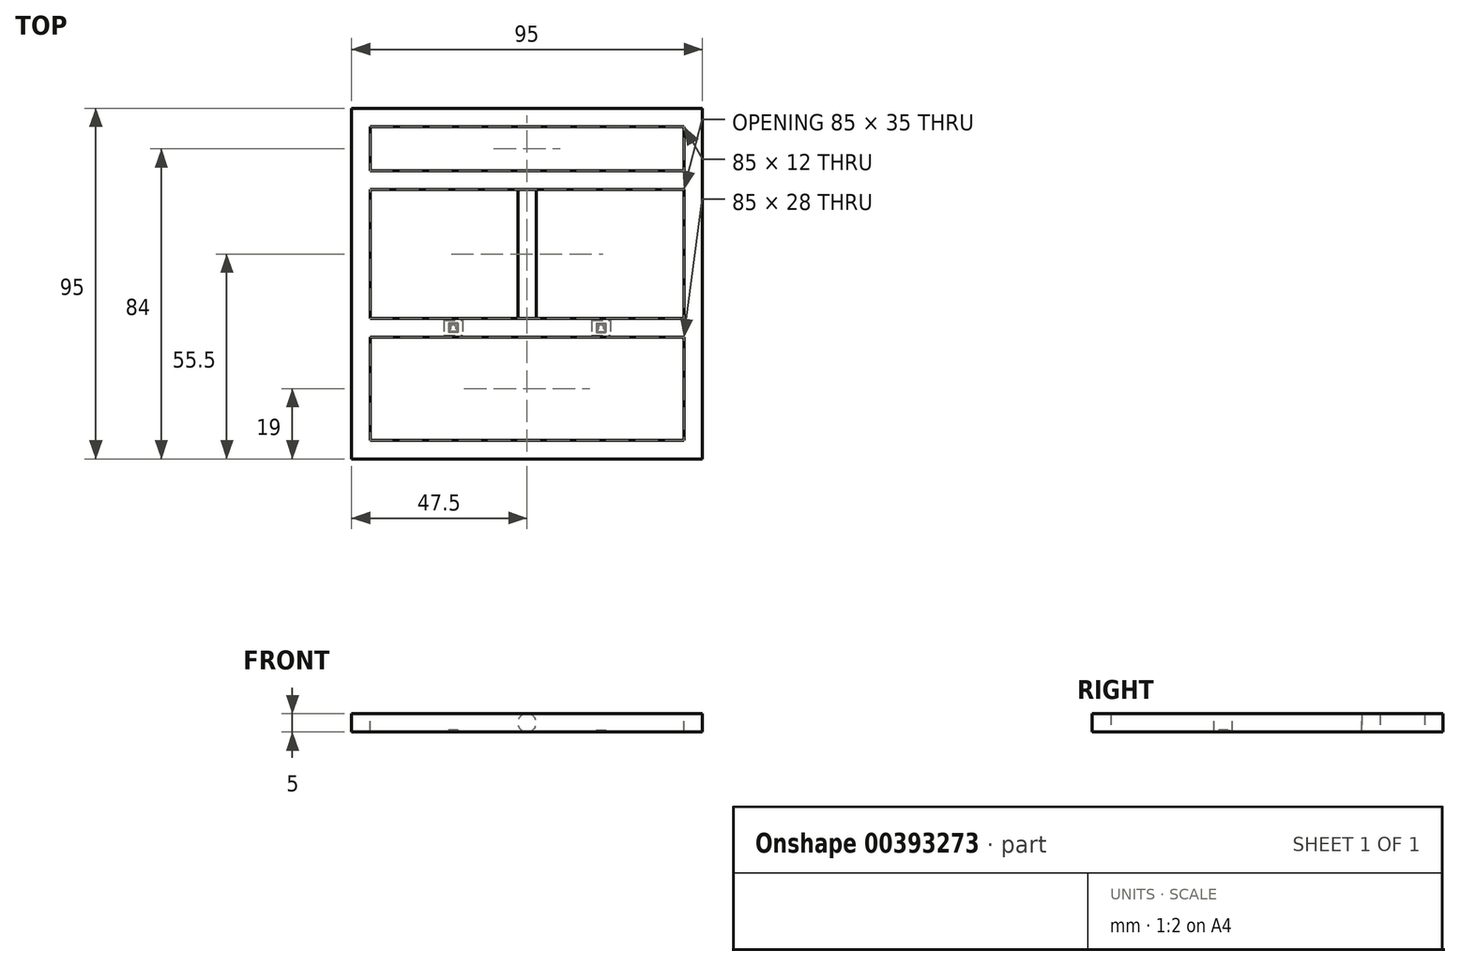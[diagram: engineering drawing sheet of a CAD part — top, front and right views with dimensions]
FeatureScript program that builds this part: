
annotation { "Feature Type Name" : "Feature", "Feature Type Description" : "" }
export const myFeature = defineFeature(function(context is Context, id is Id, definition is map)
    precondition{}
    {
        {
            var Q0;
            Q0=qCreatedBy(makeId("Front.planeOp"),FACE);
            var sketch = newSketch(context, id + "F0", { "sketchPlane" : qUnion([Q0])});
            skLineSegment(sketch, "E0.bottom", {"start": v(2.5, -2.5) * mm, "end": v(-2.5, -2.5) * mm});
            skLineSegment(sketch, "E0.top", {"start": v(2.5, 2.5) * mm, "end": v(-2.5, 2.5) * mm});
            skLineSegment(sketch, "E0.left", {"start": v(2.5, -2.5) * mm, "end": v(2.5, 2.5) * mm});
            skLineSegment(sketch, "E0.right", {"start": v(-2.5, -2.5) * mm, "end": v(-2.5, 2.5) * mm});
            skPoint(sketch, "E0.middle", {"position": v(0, 0) * mm});
            skSolve(sketch);
        }
        {
            var Q0;
            Q0 = qSketchRegion(id + "F0", true);
            extrude(context, id + "F1", {"entities" : qUnion([Q0]), "oppositeDirection" : true, "depth" : 90 * mm});
        }
        {
            var Q0;
            Q0=makeQuery(id+"F1.opExtrude","SWEPT_FACE",FACE,{"disambiguationData":[OSD([sQuery(id+"F0.wireOp",EDGE,"E0.right")])]});
            var sketch = newSketch(context, id + "F2", { "sketchPlane" : qUnion([Q0])});
            skLineSegment(sketch, "E1.bottom", {"start": v(-90, 2.5) * mm, "end": v(-85, 2.5) * mm});
            skLineSegment(sketch, "E1.top", {"start": v(-90, -2.5) * mm, "end": v(-85, -2.5) * mm});
            skLineSegment(sketch, "E1.left", {"start": v(-90, 2.5) * mm, "end": v(-90, -2.5) * mm});
            skLineSegment(sketch, "E1.right", {"start": v(-85, 2.5) * mm, "end": v(-85, -2.5) * mm});
            skSolve(sketch);
        }
        {
            var Q0;
            Q0 = qSketchRegion(id + "F2", true);
            extrude(context, id + "F3", {"entities" : qUnion([Q0]), "operationType" : NewBodyOperationType.ADD, "depth" : 90 * mm});
        }
        {
            var Q0;
            Q0=makeQuery(id+"F3.opExtrude","SWEPT_FACE",FACE,{"disambiguationData":[OSD([sQuery(id+"F2.wireOp",EDGE,"E1.right")])]});
            var sketch = newSketch(context, id + "F4", { "sketchPlane" : qUnion([Q0])});
            skLineSegment(sketch, "E2.bottom", {"start": v(-92.5, 2.5) * mm, "end": v(-87.5, 2.5) * mm});
            skLineSegment(sketch, "E2.top", {"start": v(-92.5, -2.5) * mm, "end": v(-87.5, -2.5) * mm});
            skLineSegment(sketch, "E2.left", {"start": v(-92.5, 2.5) * mm, "end": v(-92.5, -2.5) * mm});
            skLineSegment(sketch, "E2.right", {"start": v(-87.5, 2.5) * mm, "end": v(-87.5, -2.5) * mm});
            skSolve(sketch);
        }
        {
            var Q0;
            Q0 = qSketchRegion(id + "F4", true);
            extrude(context, id + "F5", {"entities" : qUnion([Q0]), "operationType" : NewBodyOperationType.ADD, "depth" : 90 * mm});
        }
        {
            var Q0;
            Q0=makeQuery(id+"F5.opExtrude","SWEPT_FACE",FACE,{"disambiguationData":[OSD([sQuery(id+"F4.wireOp",EDGE,"E2.right")])]});
            var sketch = newSketch(context, id + "F6", { "sketchPlane" : qUnion([Q0])});
            skLineSegment(sketch, "E3.bottom", {"start": v(-5, 2.5) * mm, "end": v(0, 2.5) * mm});
            skLineSegment(sketch, "E3.top", {"start": v(-5, -2.5) * mm, "end": v(0, -2.5) * mm});
            skLineSegment(sketch, "E3.left", {"start": v(-5, 2.5) * mm, "end": v(-5, -2.5) * mm});
            skLineSegment(sketch, "E3.right", {"start": v(0, 2.5) * mm, "end": v(0, -2.5) * mm});
            skSolve(sketch);
        }
        {
            var Q0;
            Q0 = qSketchRegion(id + "F6", true);
            extrude(context, id + "F7", {"entities" : qUnion([Q0]), "operationType" : NewBodyOperationType.ADD, "depth" : 90 * mm});
        }
        {
            var Q0;
            Q0=makeQuery(id+"F5.opExtrude","SWEPT_FACE",FACE,{"disambiguationData":[OSD([sQuery(id+"F4.wireOp",EDGE,"E2.right")])]});
            var sketch = newSketch(context, id + "F8", { "sketchPlane" : qUnion([Q0])});
            skLineSegment(sketch, "E4.bottom", {"start": v(68, -2.5) * mm, "end": v(73, -2.5) * mm});
            skLineSegment(sketch, "E4.top", {"start": v(68, 2.5) * mm, "end": v(73, 2.5) * mm});
            skLineSegment(sketch, "E4.left", {"start": v(68, -2.5) * mm, "end": v(68, 2.5) * mm});
            skLineSegment(sketch, "E4.right", {"start": v(73, -2.5) * mm, "end": v(73, 2.5) * mm});
            skPoint(sketch, "E4.middle", {"position": v(70.5, 0) * mm});
            skPoint(sketch, "E4.middle.positionSnap0", {"position": v(85, 0) * mm});
            skPoint(sketch, "E4.centerSnap0", {"position": v(85, 0) * mm});
            skSolve(sketch);
        }
        {
            var Q0;
            Q0 = qSketchRegion(id + "F8", true);
            extrude(context, id + "F9", {"entities" : qUnion([Q0]), "operationType" : NewBodyOperationType.ADD, "depth" : 90 * mm});
        }
        {
            var Q0;
            Q0=makeQuery(id+"F9.opExtrude","SWEPT_FACE",FACE,{"disambiguationData":[OSD([sQuery(id+"F8.wireOp",EDGE,"E4.left")])]});
            var sketch = newSketch(context, id + "F10", { "sketchPlane" : qUnion([Q0])});
            skPoint(sketch, "E5.middle.positionSnap0", {"position": v(-45, 2.5) * mm});
            skPoint(sketch, "E5.middle.positionSnap1", {"position": v(-87.5, 0) * mm});
            skPoint(sketch, "E5.centerSnap0", {"position": v(-45, 2.5) * mm});
            skPoint(sketch, "E5.centerSnap1", {"position": v(-87.5, 0) * mm});
            skCircle(sketch, "E6", {"center": v(-45, 0) * mm, "radius": 2.5 * mm});
            skSolve(sketch);
        }
        {
            var Q0;
            Q0 = qSketchRegion(id + "F10", true);
            extrude(context, id + "F11", {"entities" : qUnion([Q0]), "operationType" : NewBodyOperationType.ADD, "depth" : 35 * mm});
        }
        {
            var Q0;
            Q0=makeQuery(id+"F9.boolean.opBoolean","SPLIT",FACE,{"disambiguationData":[TD([makeQuery(id+"F7.opExtrude","SWEPT_FACE",FACE,{"disambiguationData":[OSD([sQuery(id+"F6.wireOp",EDGE,"E3.right")])]})])],"derivedFrom":makeQuery(id+"F5.opExtrude","SWEPT_FACE",FACE,{"disambiguationData":[OSD([sQuery(id+"F4.wireOp",EDGE,"E2.right")])]})});
            var sketch = newSketch(context, id + "F12", { "sketchPlane" : qUnion([Q0])});
            skLineSegment(sketch, "E7.bottom", {"start": v(33, -2.5) * mm, "end": v(28, -2.5) * mm});
            skLineSegment(sketch, "E7.top", {"start": v(33, 2.5) * mm, "end": v(28, 2.5) * mm});
            skLineSegment(sketch, "E7.left", {"start": v(33, -2.5) * mm, "end": v(33, 2.5) * mm});
            skLineSegment(sketch, "E7.right", {"start": v(28, -2.5) * mm, "end": v(28, 2.5) * mm});
            skPoint(sketch, "E7.middle", {"position": v(30.5, 0) * mm});
            skSolve(sketch);
        }
        {
            var Q0;
            Q0 = qSketchRegion(id + "F12", true);
            extrude(context, id + "F13", {"entities" : qUnion([Q0]), "operationType" : NewBodyOperationType.ADD, "depth" : 85 * mm});
        }
        {
            var Q0;
            Q0=makeQuery(id+"F13.boolean.opBoolean","MERGE",FACE,{"derivedFrom":[makeQuery(id+"F9.boolean.opBoolean","MERGE",FACE,{"derivedFrom":[makeQuery(id+"F7.boolean.opBoolean","MERGE",FACE,{"derivedFrom":[makeQuery(id+"F5.boolean.opBoolean","MERGE",FACE,{"derivedFrom":[makeQuery(id+"F3.boolean.opBoolean","MERGE",FACE,{"derivedFrom":[makeQuery(id+"F1.opExtrude","SWEPT_FACE",FACE,{"disambiguationData":[OSD([sQuery(id+"F0.wireOp",EDGE,"E0.bottom")])]}),makeQuery(id+"F3.opExtrude","SWEPT_FACE",FACE,{"disambiguationData":[OSD([sQuery(id+"F2.wireOp",EDGE,"E1.top")])]})]}),makeQuery(id+"F5.opExtrude","SWEPT_FACE",FACE,{"disambiguationData":[OSD([sQuery(id+"F4.wireOp",EDGE,"E2.top")])]})]}),makeQuery(id+"F7.opExtrude","SWEPT_FACE",FACE,{"disambiguationData":[OSD([sQuery(id+"F6.wireOp",EDGE,"E3.top")])]})]}),makeQuery(id+"F9.opExtrude","SWEPT_FACE",FACE,{"disambiguationData":[OSD([sQuery(id+"F8.wireOp",EDGE,"E4.bottom")])]})]}),makeQuery(id+"F13.opExtrude","SWEPT_FACE",FACE,{"disambiguationData":[OSD([sQuery(id+"F12.wireOp",EDGE,"E7.bottom")])]})]});
            var sketch = newSketch(context, id + "F14", { "sketchPlane" : qUnion([Q0])});
            skLineSegment(sketch, "E8.bottom", {"start": v(-67.5, -32.5) * mm, "end": v(-62.5, -32.5) * mm});
            skLineSegment(sketch, "E8.top", {"start": v(-67.5, -28.5) * mm, "end": v(-62.5, -28.5) * mm});
            skLineSegment(sketch, "E8.left", {"start": v(-67.5, -32.5) * mm, "end": v(-67.5, -28.5) * mm});
            skLineSegment(sketch, "E8.right", {"start": v(-62.5, -32.5) * mm, "end": v(-62.5, -28.5) * mm});
            skPoint(sketch, "E8.middle", {"position": v(-65, -30.5) * mm});
            skLineSegment(sketch, "E9.bottom", {"start": v(-27.5, -32.5) * mm, "end": v(-22.5, -32.5) * mm});
            skLineSegment(sketch, "E9.top", {"start": v(-27.5, -28.5) * mm, "end": v(-22.5, -28.5) * mm});
            skLineSegment(sketch, "E9.left", {"start": v(-27.5, -32.5) * mm, "end": v(-27.5, -28.5) * mm});
            skLineSegment(sketch, "E9.right", {"start": v(-22.5, -32.5) * mm, "end": v(-22.5, -28.5) * mm});
            skPoint(sketch, "E9.middle", {"position": v(-25, -30.5) * mm});
            skSolve(sketch);
        }
        {
            var Q0;
            Q0 = qSketchRegion(id + "F14", true);
            extrude(context, id + "F15", {"entities" : qUnion([Q0]), "operationType" : NewBodyOperationType.REMOVE, "oppositeDirection" : true, "depth" : 0.3 * mm});
        }
        {
            var Q0;
            Q0=makeQuery(id+"F15.boolean.opBoolean","COPY",FACE,{"derivedFrom":makeQuery(id+"F15.opExtrude","CAP_FACE",FACE,{"disambiguationData":[OSD([sQuery(id+"F14.wireOp",EDGE,"E8.bottom"),sQuery(id+"F14.wireOp",EDGE,"E8.top"),sQuery(id+"F14.wireOp",EDGE,"E8.left"),sQuery(id+"F14.wireOp",EDGE,"E8.right")])],"isStart":false})});
            var sketch = newSketch(context, id + "F16", { "sketchPlane" : qUnion([Q0])});
            skCircle(sketch, "E10", {"center": v(-65, -30.5) * mm, "radius": 0.8 * mm});
            skPoint(sketch, "E10.centerSnap0", {"position": v(-62.5, -30.5) * mm});
            skPoint(sketch, "E10.centerSnap1", {"position": v(-65, -28.5) * mm});
            skSolve(sketch);
        }
        {
            var Q0;
            Q0 = qSketchRegion(id + "F16", true);
            extrude(context, id + "F17", {"entities" : qUnion([Q0]), "operationType" : NewBodyOperationType.ADD, "depth" : 0.3 * mm});
        }
        {
            var Q0;
            Q0=makeQuery(id+"F15.boolean.opBoolean","COPY",FACE,{"derivedFrom":makeQuery(id+"F15.opExtrude","CAP_FACE",FACE,{"disambiguationData":[OSD([sQuery(id+"F14.wireOp",EDGE,"E8.bottom"),sQuery(id+"F14.wireOp",EDGE,"E8.top"),sQuery(id+"F14.wireOp",EDGE,"E8.left"),sQuery(id+"F14.wireOp",EDGE,"E8.right")])],"isStart":false})});
            var sketch = newSketch(context, id + "F18", { "sketchPlane" : qUnion([Q0])});
            skLineSegment(sketch, "E11.bottom", {"start": v(-64, -31.5) * mm, "end": v(-66, -31.5) * mm});
            skLineSegment(sketch, "E11.top", {"start": v(-64, -29.5) * mm, "end": v(-66, -29.5) * mm});
            skLineSegment(sketch, "E11.left", {"start": v(-64, -31.5) * mm, "end": v(-64, -29.5) * mm});
            skLineSegment(sketch, "E11.right", {"start": v(-66, -31.5) * mm, "end": v(-66, -29.5) * mm});
            skPoint(sketch, "E11.middle", {"position": v(-65, -30.5) * mm});
            skLineSegment(sketch, "E12.bottom", {"start": v(-63.75, -31.75) * mm, "end": v(-66.25, -31.75) * mm});
            skLineSegment(sketch, "E12.top", {"start": v(-63.75, -29.25) * mm, "end": v(-66.25, -29.25) * mm});
            skLineSegment(sketch, "E12.left", {"start": v(-63.75, -31.75) * mm, "end": v(-63.75, -29.25) * mm});
            skLineSegment(sketch, "E12.right", {"start": v(-66.25, -31.75) * mm, "end": v(-66.25, -29.25) * mm});
            skSolve(sketch);
        }
        {
            var Q0;
            Q0 = qSketchRegion(id + "F18", true);
            extrude(context, id + "F19", {"entities" : qUnion([Q0]), "operationType" : NewBodyOperationType.REMOVE, "oppositeDirection" : true, "depth" : 0.3 * mm});
        }
        {
            var Q0;
            Q0=makeQuery(id+"F15.boolean.opBoolean","COPY",FACE,{"derivedFrom":makeQuery(id+"F15.opExtrude","CAP_FACE",FACE,{"disambiguationData":[OSD([sQuery(id+"F14.wireOp",EDGE,"E9.bottom"),sQuery(id+"F14.wireOp",EDGE,"E9.top"),sQuery(id+"F14.wireOp",EDGE,"E9.left"),sQuery(id+"F14.wireOp",EDGE,"E9.right")])],"isStart":false})});
            var sketch = newSketch(context, id + "F20", { "sketchPlane" : qUnion([Q0])});
            skCircle(sketch, "E13", {"center": v(-25, -30.5) * mm, "radius": 0.8 * mm});
            skPoint(sketch, "E13.centerSnap0", {"position": v(-22.5, -30.5) * mm});
            skPoint(sketch, "E13.centerSnap1", {"position": v(-25, -28.5) * mm});
            skSolve(sketch);
        }
        {
            var Q0;
            Q0 = qSketchRegion(id + "F20", true);
            extrude(context, id + "F21", {"entities" : qUnion([Q0]), "operationType" : NewBodyOperationType.ADD, "depth" : 0.3 * mm});
        }
        {
            var Q0;
            Q0=makeQuery(id+"F15.boolean.opBoolean","COPY",FACE,{"derivedFrom":makeQuery(id+"F15.opExtrude","CAP_FACE",FACE,{"disambiguationData":[OSD([sQuery(id+"F14.wireOp",EDGE,"E9.bottom"),sQuery(id+"F14.wireOp",EDGE,"E9.top"),sQuery(id+"F14.wireOp",EDGE,"E9.left"),sQuery(id+"F14.wireOp",EDGE,"E9.right")])],"isStart":false})});
            var sketch = newSketch(context, id + "F22", { "sketchPlane" : qUnion([Q0])});
            skLineSegment(sketch, "E14.bottom", {"start": v(-26, -31.5) * mm, "end": v(-24, -31.5) * mm});
            skLineSegment(sketch, "E14.top", {"start": v(-26, -29.5) * mm, "end": v(-24, -29.5) * mm});
            skLineSegment(sketch, "E14.left", {"start": v(-26, -31.5) * mm, "end": v(-26, -29.5) * mm});
            skLineSegment(sketch, "E14.right", {"start": v(-24, -31.5) * mm, "end": v(-24, -29.5) * mm});
            skPoint(sketch, "E14.middle", {"position": v(-25, -30.5) * mm});
            skLineSegment(sketch, "E15.bottom", {"start": v(-26.25, -31.75) * mm, "end": v(-23.75, -31.75) * mm});
            skLineSegment(sketch, "E15.top", {"start": v(-26.25, -29.25) * mm, "end": v(-23.75, -29.25) * mm});
            skLineSegment(sketch, "E15.left", {"start": v(-26.25, -31.75) * mm, "end": v(-26.25, -29.25) * mm});
            skLineSegment(sketch, "E15.right", {"start": v(-23.75, -31.75) * mm, "end": v(-23.75, -29.25) * mm});
            skSolve(sketch);
        }
        {
            var Q0;
            Q0 = qSketchRegion(id + "F22", true);
            extrude(context, id + "F23", {"entities" : qUnion([Q0]), "operationType" : NewBodyOperationType.REMOVE, "oppositeDirection" : true, "depth" : 0.3 * mm});
        }
    });
